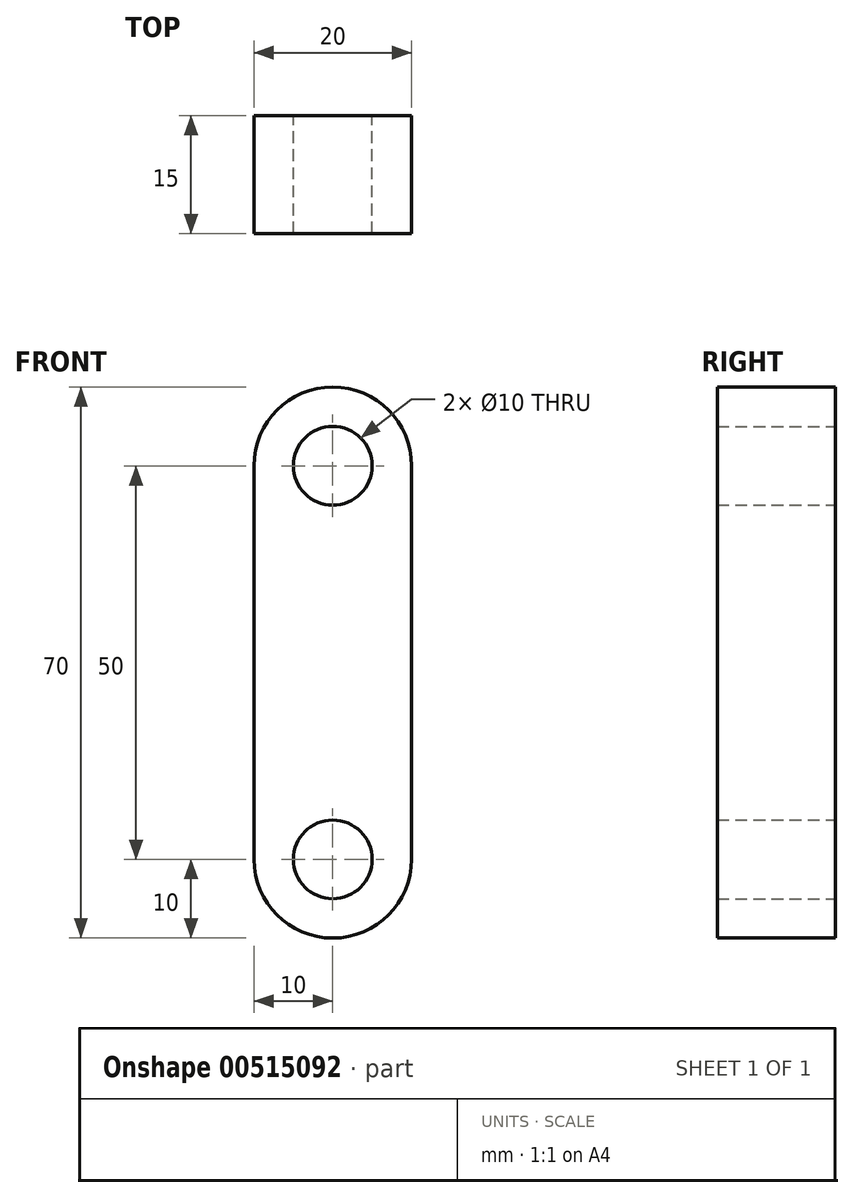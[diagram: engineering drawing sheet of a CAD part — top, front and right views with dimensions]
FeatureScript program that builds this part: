
annotation { "Feature Type Name" : "Feature", "Feature Type Description" : "" }
export const myFeature = defineFeature(function(context is Context, id is Id, definition is map)
    precondition{}
    {
        {
            var Q0;
            Q0=qCreatedBy(makeId("Front.planeOp"),FACE);
            var sketch = newSketch(context, id + "F0", { "sketchPlane" : qUnion([Q0])});
            skLineSegment(sketch, "E0.bottom", {"start": v(-10, 35) * mm, "end": v(10, 35) * mm});
            skLineSegment(sketch, "E0.top", {"start": v(-10, -35) * mm, "end": v(10, -35) * mm});
            skLineSegment(sketch, "E0.left", {"start": v(-10, 35) * mm, "end": v(-10, -35) * mm});
            skLineSegment(sketch, "E0.right", {"start": v(10, 35) * mm, "end": v(10, -35) * mm});
            skPoint(sketch, "E0.middle", {"position": v(0, 0) * mm});
            skCircle(sketch, "E1", {"center": v(0, 25) * mm, "radius": 10 * mm});
            skPoint(sketch, "E1.first.point", {"position": v(-10, 25) * mm});
            skPoint(sketch, "E1.second.point", {"position": v(0, 35) * mm});
            skPoint(sketch, "E1.third.point", {"position": v(10, 25) * mm});
            skCircle(sketch, "E2", {"center": v(0, 25) * mm, "radius": 5 * mm});
            skCircle(sketch, "E3", {"center": v(0, -25) * mm, "radius": 10 * mm});
            skPoint(sketch, "E3.first.point", {"position": v(-10, -25) * mm});
            skPoint(sketch, "E3.second.point", {"position": v(0, -35) * mm});
            skPoint(sketch, "E3.third.point", {"position": v(10, -25) * mm});
            skCircle(sketch, "E4", {"center": v(0, -25) * mm, "radius": 5 * mm});
            skSolve(sketch);
        }
        {
            var Q0;
            Q0=makeQuery(id+"F0.imprint","IMPRINT",FACE,{"disambiguationData":[TD([[makeQuery(id+"F0.imprint","IMPRINT",EDGE,{"derivedFrom":sQuery(id+"F0.wireOp",EDGE,"E2")}),-1.0]])]});
            var Q1;
            {var subQ0=sQuery(id+"F0.wireOp",EDGE,"E1");var subQ1=sQuery(id+"F0.wireOp",EDGE,"E0.left");var subQ2=makeQuery(id+"F0.imprint","INTERSECT",VERTEX,{"derivedFrom":[subQ1,subQ0]});Q1=makeQuery(id+"F0.imprint","IMPRINT",FACE,{"disambiguationData":[TD([[makeQuery(id+"F0.imprint","IMPRINT",EDGE,{"disambiguationData":[TD([[subQ2,-1.0]])],"derivedFrom":subQ1}),1.0]])]});}
            var Q2;
            Q2=makeQuery(id+"F0.imprint","IMPRINT",FACE,{"disambiguationData":[TD([[makeQuery(id+"F0.imprint","IMPRINT",EDGE,{"derivedFrom":sQuery(id+"F0.wireOp",EDGE,"E4")}),-1.0]])]});
            extrude(context, id + "F1", {"entities" : qUnion([Q0, Q1, Q2]), "endBound" : BoundingType.SYMMETRIC, "depth" : 15 * mm, "offsetDistance" : 25.4 * mm});
        }
    });
